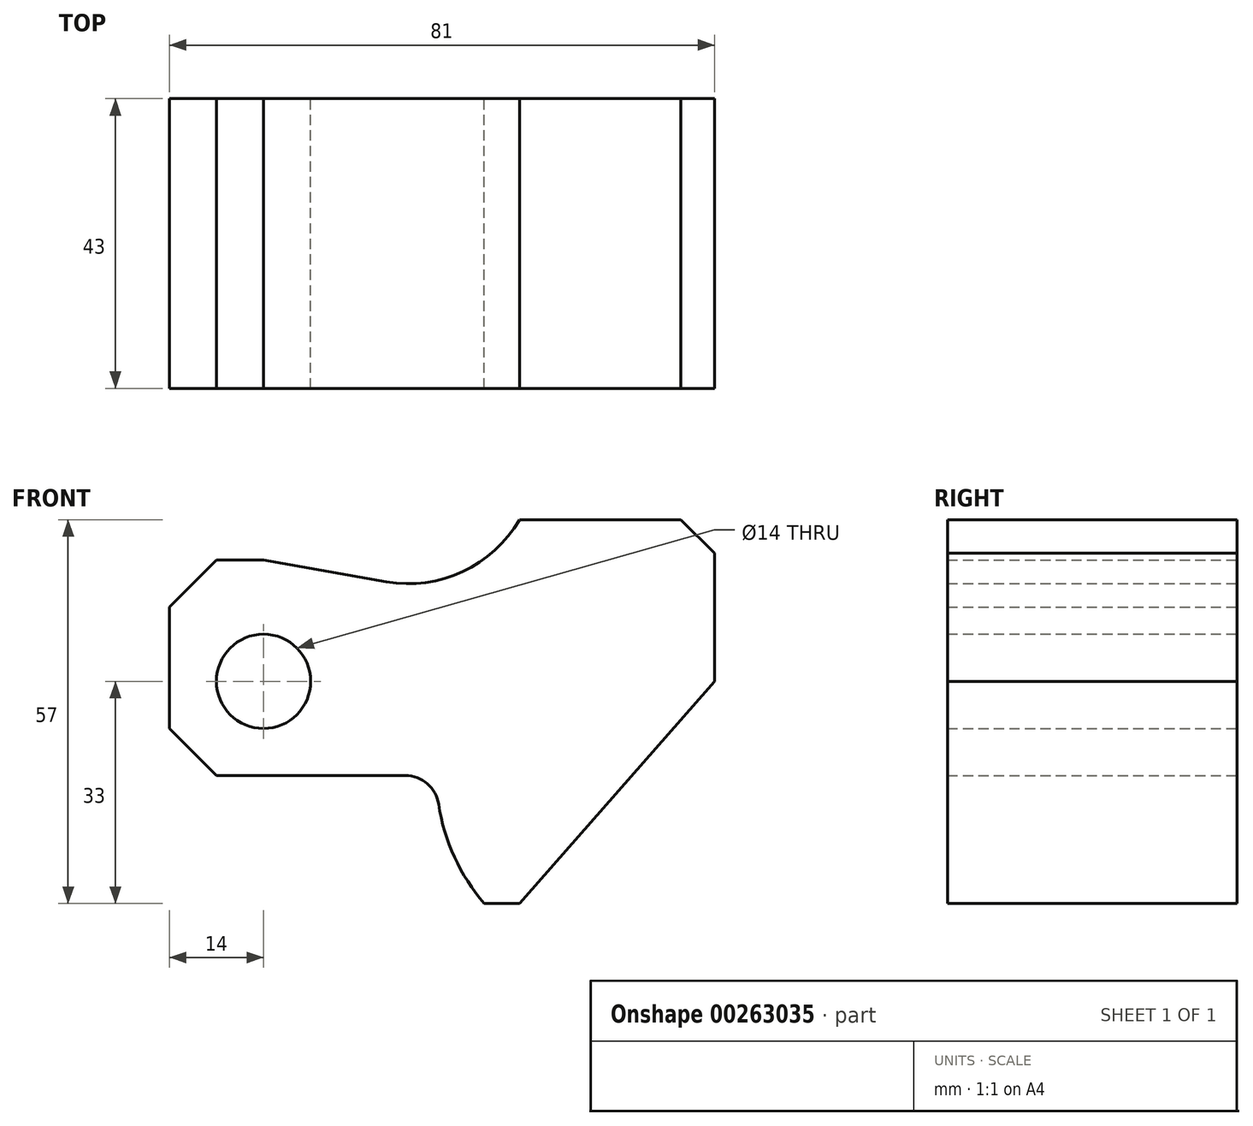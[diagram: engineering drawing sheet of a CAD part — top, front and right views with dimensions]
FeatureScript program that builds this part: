
annotation { "Feature Type Name" : "Feature", "Feature Type Description" : "" }
export const myFeature = defineFeature(function(context is Context, id is Id, definition is map)
    precondition{}
    {
        {
            var Q0;
            Q0=qCreatedBy(makeId("Front.planeOp"),FACE);
            var sketch = newSketch(context, id + "F0", { "sketchPlane" : qUnion([Q0])});
            skCircle(sketch, "E0", {"center": v(0, 0) * mm, "radius": 7 * mm});
            skLineSegment(sketch, "E1", {"start": v(-14, -7) * mm, "end": v(-14, 11) * mm});
            skLineSegment(sketch, "E2", {"start": v(0, 18) * mm, "end": v(-7, 18) * mm});
            skLineSegment(sketch, "E3", {"start": v(-14, -7) * mm, "end": v(-7, -14) * mm});
            skLineSegment(sketch, "E4", {"start": v(-7, -14) * mm, "end": v(21.07, -14) * mm});
            skArc(sketch, "E5", {"start": v(26.01, -18.26) * mm, "mid": v(24.33, -15.21) * mm, "end": v(21.07, -14) * mm});
            skLineSegment(sketch, "E6", {"start": v(67, 0) * mm, "end": v(67, 19) * mm});
            skLineSegment(sketch, "E7", {"start": v(67, 19) * mm, "end": v(62, 24) * mm});
            skLineSegment(sketch, "E8", {"start": v(62, 24) * mm, "end": v(38, 24) * mm});
            skLineSegment(sketch, "E9", {"start": v(0, 18) * mm, "end": v(18.24, 14.78) * mm});
            skArc(sketch, "E10", {"start": v(18.24, 14.78) * mm, "mid": v(29.57, 16.28) * mm, "end": v(38, 24) * mm});
            skArc(sketch, "E11", {"start": v(26.01, -18.26) * mm, "mid": v(28.35, -26.12) * mm, "end": v(32.79, -33) * mm});
            skLineSegment(sketch, "E12", {"start": v(32.79, -33) * mm, "end": v(38, -33) * mm});
            skLineSegment(sketch, "E13", {"start": v(38, -33) * mm, "end": v(67, 0) * mm});
            skLineSegment(sketch, "E14", {"start": v(-7, 18) * mm, "end": v(-14, 11) * mm});
            skSolve(sketch);
        }
        {
            var Q0;
            Q0=makeQuery(id+"F0.imprint","IMPRINT",FACE,{"disambiguationData":[TD([[makeQuery(id+"F0.imprint","IMPRINT",EDGE,{"derivedFrom":sQuery(id+"F0.wireOp",EDGE,"E0")}),-1.0]])]});
            extrude(context, id + "F1", {"entities" : qUnion([Q0]), "endBound" : BoundingType.SYMMETRIC, "depth" : 43 * mm});
        }
    });
